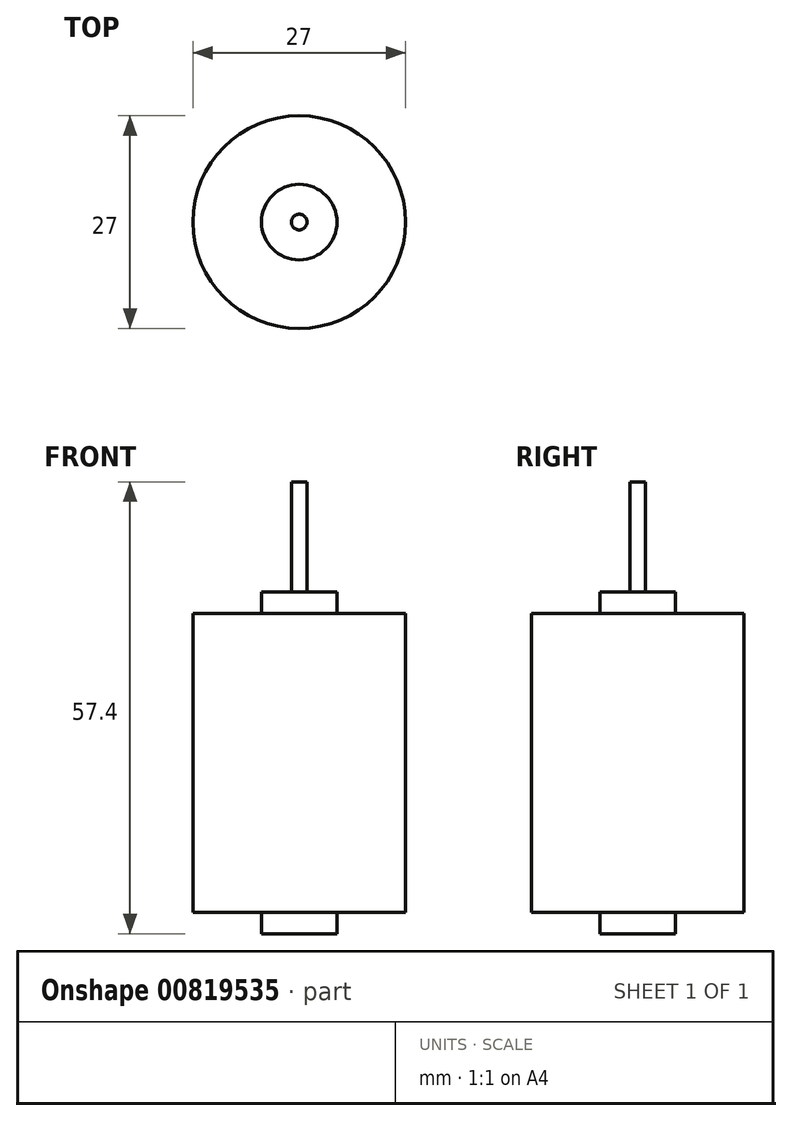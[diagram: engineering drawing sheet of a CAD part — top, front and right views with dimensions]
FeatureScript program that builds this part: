
annotation { "Feature Type Name" : "Feature", "Feature Type Description" : "" }
export const myFeature = defineFeature(function(context is Context, id is Id, definition is map)
    precondition{}
    {
        {
            var Q0;
            Q0=qCreatedBy(makeId("Front.planeOp"),FACE);
            var sketch = newSketch(context, id + "F0", { "sketchPlane" : qUnion([Q0])});
            skLineSegment(sketch, "E0", {"start": v(-38.63, -22.65) * mm, "end": v(-33.83, -22.65) * mm});
            skLineSegment(sketch, "E1", {"start": v(-33.83, -19.95) * mm, "end": v(-25.13, -19.95) * mm});
            skLineSegment(sketch, "E2", {"start": v(-25.13, -19.95) * mm, "end": v(-25.13, 18.05) * mm});
            skLineSegment(sketch, "E3", {"start": v(-25.13, 18.05) * mm, "end": v(-33.83, 18.05) * mm});
            skLineSegment(sketch, "E4", {"start": v(-33.83, 18.05) * mm, "end": v(-33.83, 20.75) * mm});
            skLineSegment(sketch, "E5", {"start": v(-33.83, -22.65) * mm, "end": v(-33.83, -19.95) * mm});
            skLineSegment(sketch, "E6", {"start": v(-33.83, 20.75) * mm, "end": v(-37.63, 20.75) * mm});
            skLineSegment(sketch, "E7", {"start": v(-38.63, -22.65) * mm, "end": v(-38.63, 34.75) * mm});
            skLineSegment(sketch, "E8", {"start": v(-37.63, 20.75) * mm, "end": v(-37.63, 34.75) * mm});
            skLineSegment(sketch, "E9", {"start": v(-38.63, 34.75) * mm, "end": v(-37.63, 34.75) * mm});
            skSolve(sketch);
        }
        {
            var Q0;
            Q0 = qSketchRegion(id + "F0", true);
            var Q1;
            Q1=sQuery(id+"F0.wireOp",EDGE,"E7");
            revolve(context, id + "F1", {"surfaceOperationType" : NewSurfaceOperationType.NEW, "entities" : qUnion([Q0]), "axis" : qUnion([Q1]), "revolveType" : RevolveType.FULL});
        }
    });
